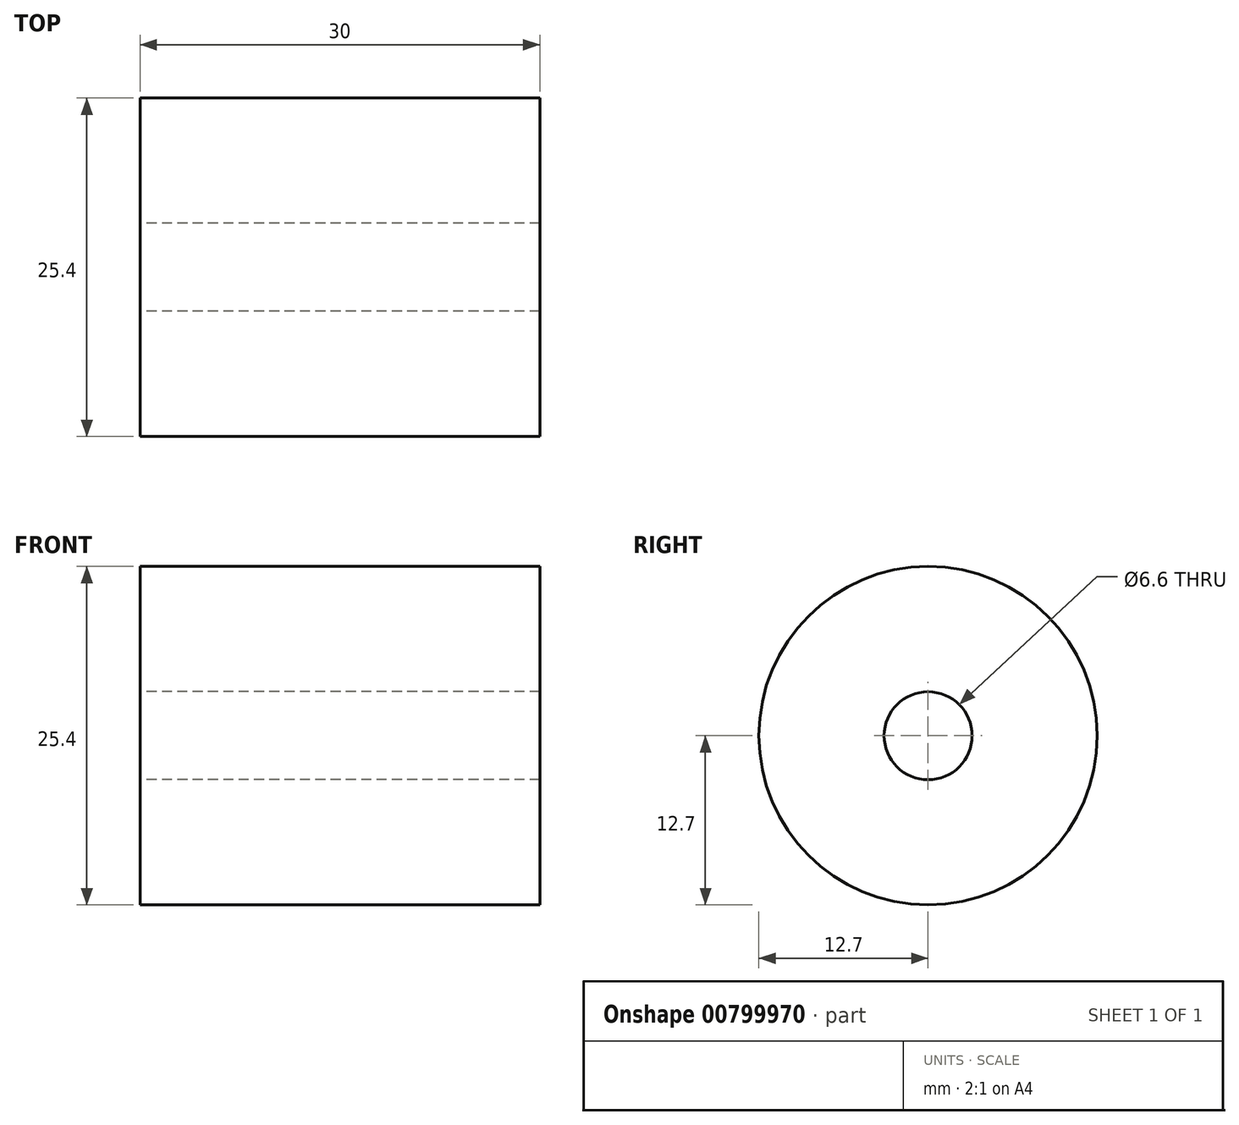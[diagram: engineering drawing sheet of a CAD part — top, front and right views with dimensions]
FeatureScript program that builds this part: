
annotation { "Feature Type Name" : "Feature", "Feature Type Description" : "" }
export const myFeature = defineFeature(function(context is Context, id is Id, definition is map)
    precondition{}
    {
        {
            var Q0;
            Q0=qCreatedBy(makeId("Right.planeOp"),FACE);
            var sketch = newSketch(context, id + "F0", { "sketchPlane" : qUnion([Q0])});
            skCircle(sketch, "E0", {"center": v(0, 0) * mm, "radius": 12.7 * mm});
            skSolve(sketch);
        }
        {
            var Q0;
            Q0 = qSketchRegion(id + "F0", true);
            extrude(context, id + "F1", {"entities" : qUnion([Q0]), "depth" : 30 * mm, "offsetDistance" : 25 * mm});
        }
        {
            var Q0;
            Q0=makeQuery(id+"F1.opExtrude","CAP_FACE",FACE,{"disambiguationData":[OSD([sQuery(id+"F0.wireOp",EDGE,"E0")])],"isStart":true});
            var sketch = newSketch(context, id + "F2", { "sketchPlane" : qUnion([Q0])});
            skPoint(sketch, "E1", {"position": v(0, 0) * mm});
            skSolve(sketch);
        }
        {
            var Q0;
            Q0=sQuery(id+"F2.wireOp",VERTEX,"E1");
            var Q1;
            Q1=makeQuery(id+"F1.opExtrude","SWEPT_BODY",BODY,{"disambiguationData":[OSD([sQuery(id+"F0.wireOp",EDGE,"E0")])]});
            hole(context, id + "F3", {"style" : HoleStyle.SIMPLE, "endStyle" : HoleEndStyle.THROUGH, "standardTappedOrClearance" : lookupTablePath({ "standard" : "ISO", "fit" : "Normal", "size" : "M6", "type" : "Clearance" }), "standardBlindInLast" : lookupTablePath({ "fit" : "Standard", "standard" : "ISO", "size" : "M6", "type" : "Clearance" }), "holeDiameter" : 6.6 * mm, "majorDiameter" : 5 * mm, "isTappedThrough" : true, "tappedDepth" : 12 * mm, "tapClearance" : 3, "locations" : qUnion([Q0]), "scope" : qUnion([Q1])});
        }
    });
